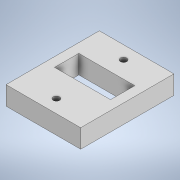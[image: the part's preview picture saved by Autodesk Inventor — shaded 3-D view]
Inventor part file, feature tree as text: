
AUTODESK INVENTOR PART (.ipt)
format: ipt  version: 2020.3 (Build 243373000, 373)  size: 241,664 bytes
history: native  units: mm
features: extrude x1, sketch x1
ambient origin geometry x8: Origin, YZ Plane, XZ Plane, XY Plane, X Axis, Y Axis, Z Axis, Center Point
bodies: Solid1 (feature_tree)
feature tree (2):
  extrude  "Extrusion1"  Depth=50.0mm
  sketch  "Sketch1"  dims[d0=40.0mm d1=50.0mm d2=3.4mm d3=3.4mm d4=10.0mm d5=0.0mm d6=19.0mm]
